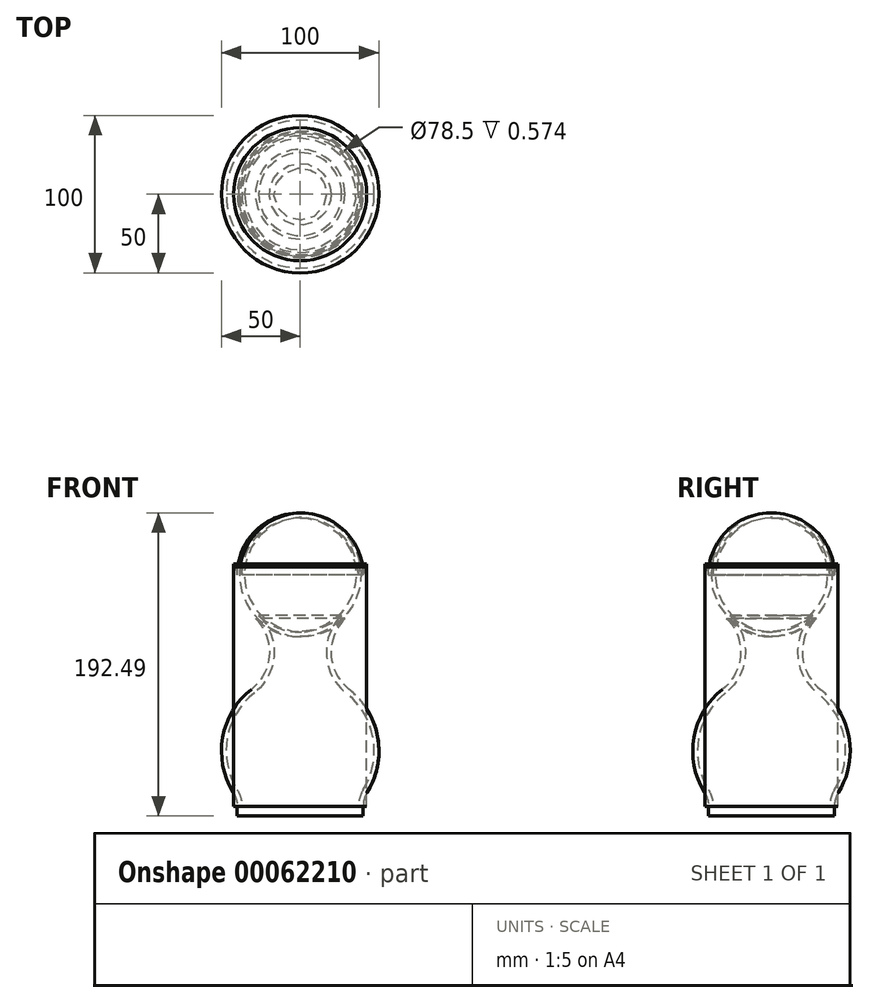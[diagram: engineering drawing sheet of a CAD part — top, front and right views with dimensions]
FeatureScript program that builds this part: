
annotation { "Feature Type Name" : "Feature", "Feature Type Description" : "" }
export const myFeature = defineFeature(function(context is Context, id is Id, definition is map)
    precondition{}
    {
        {
            var Q0;
            Q0=qCreatedBy(makeId("Front.planeOp"),FACE);
            var sketch = newSketch(context, id + "F0", { "sketchPlane" : qUnion([Q0])});
            skArc(sketch, "E0", {"start": v(-31, 80.56) * mm, "mid": v(-49.23, 50.04) * mm, "end": v(-42.58, 15.12) * mm});
            skLineSegment(sketch, "E1", {"start": v(-49.62, 47.47) * mm, "end": v(-49.62, 103.1) * mm, "construction": true});
            skArc(sketch, "E2", {"start": v(-31, 80.56) * mm, "mid": v(-19.63, 102.41) * mm, "end": v(-28.43, 125.42) * mm});
            skLineSegment(sketch, "E3.rect.right", {"start": v(-40, 6) * mm, "end": v(-40, 0) * mm});
            skPoint(sketch, "E3.rect.middle", {"position": v(0, 0) * mm});
            skLineSegment(sketch, "E4", {"start": v(-40, 0) * mm, "end": v(0, 0) * mm});
            skArc(sketch, "E5", {"start": v(-40, 6) * mm, "mid": v(-40.66, 10.74) * mm, "end": v(-42.58, 15.12) * mm});
            skLineSegment(sketch, "E6", {"start": v(-40, 6) * mm, "end": v(-40, 172.73) * mm, "construction": true});
            skLineSegment(sketch, "E7.bottom", {"start": v(-40, 160) * mm, "end": v(0, 160) * mm});
            skLineSegment(sketch, "E7.top", {"start": v(-0.75, 153.24) * mm, "end": v(0, 153.24) * mm});
            skArc(sketch, "E8", {"start": v(-40, 153.24) * mm, "mid": v(-37, 138.18) * mm, "end": v(-28.43, 125.42) * mm});
            skLineSegment(sketch, "E9", {"start": v(0, 0) * mm, "end": v(0, 160) * mm, "construction": true});
            skPoint(sketch, "E9.endSnap0", {"position": v(0, 160) * mm});
            skPoint(sketch, "E7.right.start.orphan", {"position": v(40, 160) * mm});
            skLineSegment(sketch, "E10", {"start": v(0, 160) * mm, "end": v(0, 0) * mm});
            skArc(sketch, "E11", {"start": v(-40, 153.24) * mm, "mid": v(-40.59, 155.97) * mm, "end": v(-42.25, 158.22) * mm});
            skLineSegment(sketch, "E12", {"start": v(-42.25, 158.22) * mm, "end": v(-42.25, 160) * mm});
            skLineSegment(sketch, "E13", {"start": v(-42.25, 160) * mm, "end": v(-40, 160) * mm});
            skLineSegment(sketch, "E14", {"start": v(-50, 89.95) * mm, "end": v(-50, -7.3) * mm, "construction": true});
            skPoint(sketch, "E15", {"position": v(-50, 41.33) * mm});
            skLineSegment(sketch, "E16", {"start": v(-19.58, 157.4) * mm, "end": v(-19.58, 50.85) * mm, "construction": true});
            skPoint(sketch, "E17", {"position": v(-19.58, 104.13) * mm});
            skSolve(sketch);
        }
        {
            var Q0;
            Q0=makeQuery(id+"F0.imprint","IMPRINT",FACE,{"disambiguationData":[TD([[makeQuery(id+"F0.imprint","IMPRINT",EDGE,{"derivedFrom":sQuery(id+"F0.wireOp",EDGE,"E0")}),1.0]])]});
            var Q1;
            Q1=sQuery(id+"F0.wireOp",EDGE,"E10");
            revolve(context, id + "F1", {"entities" : qUnion([Q0]), "axis" : qUnion([Q1]), "revolveType" : RevolveType.FULL});
        }
        {
            var Q0;
            Q0=makeQuery(id+"F1.opRevolve","SWEPT_FACE",FACE,{"disambiguationData":[OSD([sQuery(id+"F0.wireOp",EDGE,"E7.bottom"),sQuery(id+"F0.wireOp",EDGE,"E13")])]});
            shell(context, id + "F2", {"entities" : qUnion([Q0]), "thickness" : 3 * mm});
        }
        {
            var Q0;
            Q0=makeQuery(id+"F1.opRevolve","SWEPT_FACE",FACE,{"disambiguationData":[OSD([sQuery(id+"F0.wireOp",EDGE,"E4")])]});
            extrude(context, id + "F3", {"entities" : qUnion([Q0]), "operationType" : NewBodyOperationType.ADD, "oppositeDirection" : true, "depth" : 6 * mm});
        }
        {
            var Q0;
            Q0=qCreatedBy(makeId("Front.planeOp"),FACE);
            var sketch = newSketch(context, id + "F4", { "sketchPlane" : qUnion([Q0])});
            skLineSegment(sketch, "E18.0", {"start": v(-40, 6) * mm, "end": v(40, 6) * mm});
            skLineSegment(sketch, "E19.1", {"start": v(-42.25, 160) * mm, "end": v(42.25, 160) * mm});
            skLineSegment(sketch, "E20", {"start": v(-42.25, 160) * mm, "end": v(-42.25, 6) * mm});
            skLineSegment(sketch, "E21", {"start": v(-42.25, 6) * mm, "end": v(42.25, 6) * mm});
            skLineSegment(sketch, "E22", {"start": v(42.25, 6) * mm, "end": v(42.25, 160) * mm});
            skLineSegment(sketch, "E23", {"start": v(0, 160) * mm, "end": v(0, 6) * mm});
            skSolve(sketch);
        }
        {
            var Q0;
            {var subQ2=sQuery(id+"F4.wireOp",EDGE,"E20");Q0=makeQuery(id+"F4.imprint","IMPRINT",FACE,{"disambiguationData":[TD([[makeQuery(id+"F4.imprint","IMPRINT",EDGE,{"derivedFrom":subQ2}),1.0]])]});}
            var Q1;
            Q1=sQuery(id+"F4.wireOp",EDGE,"E23");
            revolve(context, id + "F5", {"entities" : qUnion([Q0]), "axis" : qUnion([Q1]), "revolveType" : RevolveType.FULL});
        }
    });
